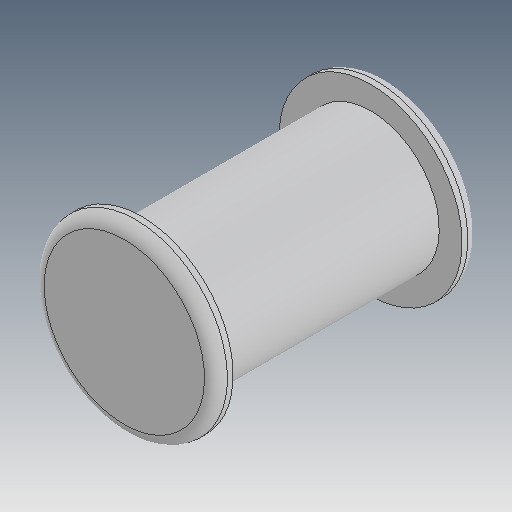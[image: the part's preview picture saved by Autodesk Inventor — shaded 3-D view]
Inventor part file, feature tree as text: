
AUTODESK INVENTOR PART (.ipt)
format: ipt  version: 2017 (Build 210142000, 142)  size: 138,752 bytes
history: native  units: mm
features: revolve x1, fillet x1, mirror x1, sketch x1
ambient origin geometry x8: Origin, YZ Plane, XZ Plane, XY Plane, X Axis, Y Axis, Z Axis, Center Point
bodies: Body1 (feature_tree)
feature tree (4):
  revolve  "Revolution2"  [1 undecoded]
  fillet  "Fillet1"  Radius=4.0mm
  mirror  "Mirror1"
  sketch  "Sketch4"  dims[d32=3.0mm d33=5.0mm d35=4.0mm d36=0.75mm d37=90.0deg d41=0.5mm]
note: 1 required parameter value undecoded (feature->parameter linkage not recoverable at this tier; creation-order binding heuristic only, values carry confidence <= 0.55)
